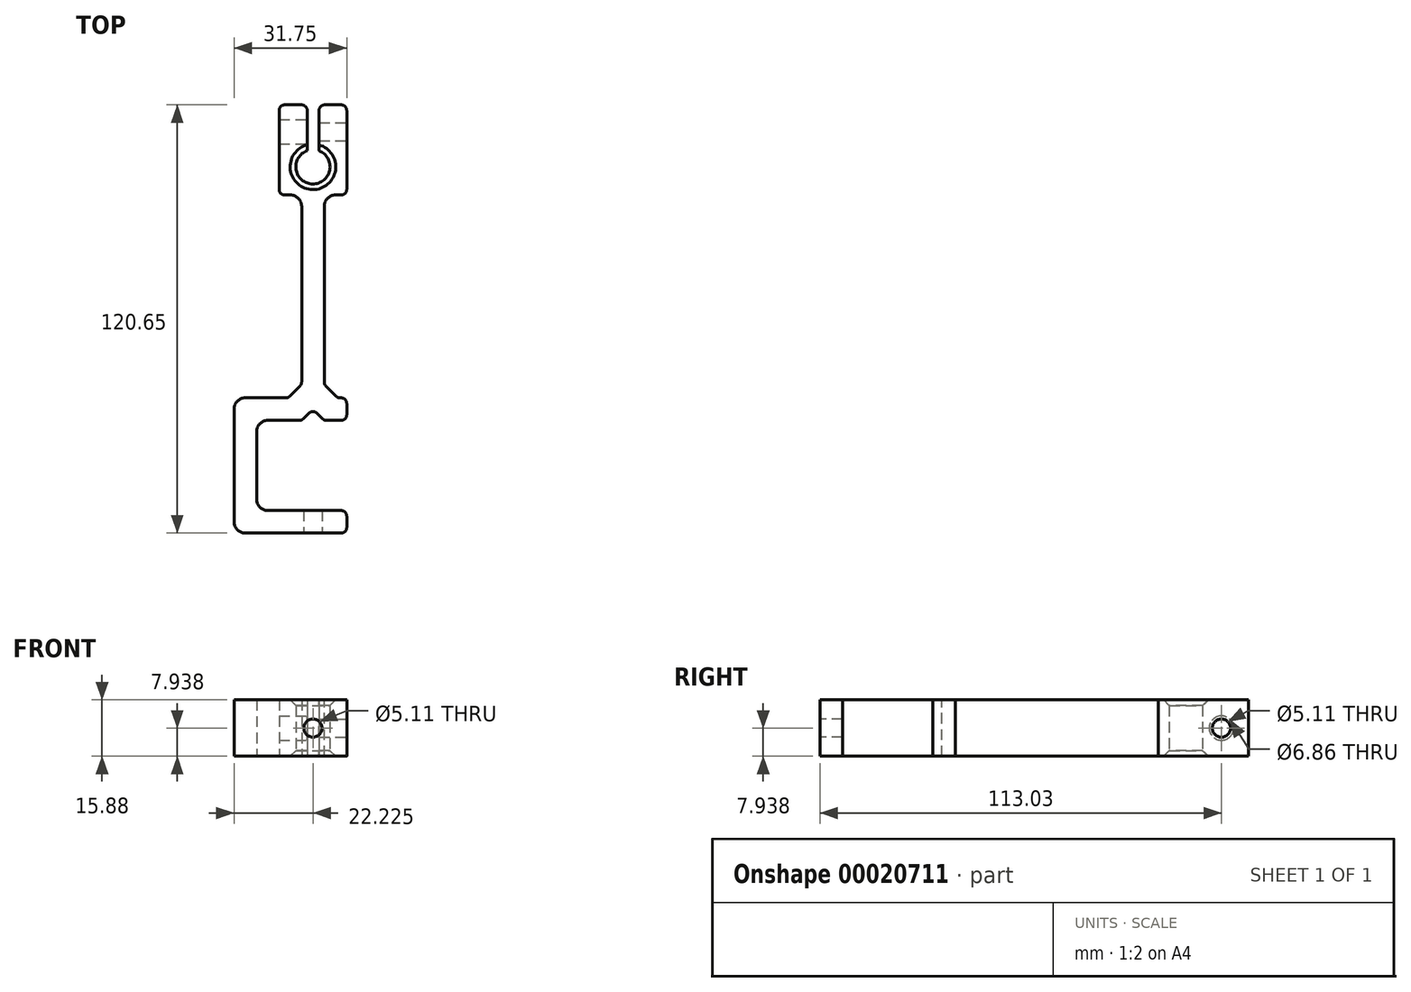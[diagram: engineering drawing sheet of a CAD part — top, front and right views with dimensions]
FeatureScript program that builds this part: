
annotation { "Feature Type Name" : "Feature", "Feature Type Description" : "" }
export const myFeature = defineFeature(function(context is Context, id is Id, definition is map)
    precondition{}
    {
        {
            var Q0;
            Q0=qCreatedBy(makeId("Top.planeOp"),FACE);
            var sketch = newSketch(context, id + "F0", { "sketchPlane" : qUnion([Q0])});
            skLineSegment(sketch, "E0", {"start": v(0, 0) * mm, "end": v(0, 31.75) * mm});
            skLineSegment(sketch, "E1", {"start": v(6.35, 111.12) * mm, "end": v(6.35, 95.25) * mm});
            skLineSegment(sketch, "E2", {"start": v(-6.35, 38.1) * mm, "end": v(-6.35, 0) * mm});
            skLineSegment(sketch, "E3", {"start": v(-6.35, 0) * mm, "end": v(0, 0) * mm});
            skArc(sketch, "E4", {"start": v(14.29, 107.74) * mm, "mid": v(15.8, 98.36) * mm, "end": v(17.59, 107.7) * mm});
            skLineSegment(sketch, "E5", {"start": v(6.35, 95.25) * mm, "end": v(12.7, 95.25) * mm});
            skLineSegment(sketch, "E6", {"start": v(12.7, 95.25) * mm, "end": v(12.7, 38.1) * mm});
            skLineSegment(sketch, "E7", {"start": v(25.4, 95.25) * mm, "end": v(19.05, 95.25) * mm});
            skLineSegment(sketch, "E8.trimOffspring", {"start": v(25.4, 95.25) * mm, "end": v(25.4, 111.12) * mm});
            skLineSegment(sketch, "E9", {"start": v(12.7, 38.1) * mm, "end": v(-6.35, 38.1) * mm});
            skLineSegment(sketch, "E10", {"start": v(19.05, 95.25) * mm, "end": v(19.05, 38.1) * mm});
            skLineSegment(sketch, "E11", {"start": v(6.35, 111.12) * mm, "end": v(6.35, 120.65) * mm});
            skLineSegment(sketch, "E12", {"start": v(6.35, 120.65) * mm, "end": v(14.29, 120.65) * mm});
            skLineSegment(sketch, "E13", {"start": v(25.4, 120.65) * mm, "end": v(25.4, 111.12) * mm});
            skLineSegment(sketch, "E14", {"start": v(14.29, 120.65) * mm, "end": v(14.29, 107.74) * mm});
            skLineSegment(sketch, "E15", {"start": v(17.59, 120.65) * mm, "end": v(17.59, 107.7) * mm});
            skLineSegment(sketch, "E16.trimOffspring", {"start": v(17.59, 120.65) * mm, "end": v(25.4, 120.65) * mm});
            skLineSegment(sketch, "E17", {"start": v(19.05, 38.1) * mm, "end": v(25.4, 38.1) * mm});
            skLineSegment(sketch, "E18", {"start": v(25.4, 38.1) * mm, "end": v(25.4, 31.75) * mm});
            skLineSegment(sketch, "E19", {"start": v(0, 0) * mm, "end": v(25.4, 0) * mm});
            skLineSegment(sketch, "E20", {"start": v(25.4, 0) * mm, "end": v(25.4, 6.35) * mm});
            skLineSegment(sketch, "E21", {"start": v(25.4, 6.35) * mm, "end": v(0, 6.35) * mm});
            skLineSegment(sketch, "E22", {"start": v(0, 31.75) * mm, "end": v(12.7, 31.75) * mm});
            skLineSegment(sketch, "E23", {"start": v(12.7, 31.75) * mm, "end": v(15.88, 34.92) * mm});
            skLineSegment(sketch, "E24", {"start": v(15.88, 34.92) * mm, "end": v(19.05, 31.75) * mm});
            skLineSegment(sketch, "E25", {"start": v(19.05, 31.75) * mm, "end": v(25.4, 31.75) * mm});
            skSolve(sketch);
        }
        {
            var Q0;
            Q0=qSketchRegion(id+"F0",true);
            extrude(context, id + "F1", {"entities" : qUnion([Q0]), "depth" : 15.88 * mm});
        }
        {
            var Q0;
            Q0=makeQuery(id+"F1.opExtrude","SWEPT_EDGE",EDGE,{"disambiguationData":[OSD([sQuery(id+"F0.wireOp",EDGE,"E0"),sQuery(id+"F0.wireOp",EDGE,"cbf15064-4b03-4c0a-8a49-597fd69c5e20.trimOffspring")])]});
            var Q1;
            Q1=makeQuery(id+"F1.opExtrude","SWEPT_EDGE",EDGE,{"disambiguationData":[OSD([sQuery(id+"F0.wireOp",EDGE,"E0"),sQuery(id+"F0.wireOp",EDGE,"E21")])]});
            var Q2;
            Q2=makeQuery(id+"F1.opExtrude","SWEPT_EDGE",EDGE,{"disambiguationData":[OSD([sQuery(id+"F0.wireOp",EDGE,"E5"),sQuery(id+"F0.wireOp",EDGE,"E6")])]});
            var Q3;
            Q3=makeQuery(id+"F1.opExtrude","SWEPT_EDGE",EDGE,{"disambiguationData":[OSD([sQuery(id+"F0.wireOp",EDGE,"E7"),sQuery(id+"F0.wireOp",EDGE,"E10")])]});
            var Q4;
            Q4=makeQuery(id+"F1.opExtrude","SWEPT_EDGE",EDGE,{"disambiguationData":[OSD([sQuery(id+"F0.wireOp",EDGE,"E2"),sQuery(id+"F0.wireOp",EDGE,"E9")])]});
            var Q5;
            Q5=makeQuery(id+"F1.opExtrude","SWEPT_EDGE",EDGE,{"disambiguationData":[OSD([sQuery(id+"F0.wireOp",EDGE,"E2"),sQuery(id+"F0.wireOp",EDGE,"E3")])]});
            fillet(context, id + "F2", {"entities" : qUnion([Q0, Q1, Q2, Q3, Q4, Q5]), "radius" : 3.17 * mm, "tangentPropagation" : true, "allowEdgeOverflow" : false});
        }
        {
            var Q0;
            Q0=makeQuery(id+"F1.opExtrude","SWEPT_FACE",FACE,{"disambiguationData":[OSD([sQuery(id+"F0.wireOp",EDGE,"E8.trimOffspring")])]});
            var sketch = newSketch(context, id + "F3", { "sketchPlane" : qUnion([Q0])});
            skCircle(sketch, "E26", {"center": v(113.03, 7.94) * mm, "radius": 2.55 * mm});
            skSolve(sketch);
        }
        {
            var Q0;
            Q0=qSketchRegion(id+"F3",true);
            extrude(context, id + "F4", {"entities" : qUnion([Q0]), "operationType" : NewBodyOperationType.REMOVE, "endBound" : BoundingType.UP_TO_NEXT, "oppositeDirection" : true, "depth" : 6.35 * mm});
        }
        {
            var Q0;
            Q0=makeQuery(id+"F1.opExtrude","CAP_EDGE",EDGE,{"disambiguationData":[OSD([sQuery(id+"F0.wireOp",EDGE,"E4")])],"isStart":false});
            var Q1;
            Q1=makeQuery(id+"F1.opExtrude","CAP_EDGE",EDGE,{"disambiguationData":[OSD([sQuery(id+"F0.wireOp",EDGE,"E4")])],"isStart":true});
            chamfer(context, id + "F5", {"entities" : qUnion([Q0, Q1]), "width" : 1.59 * mm, "tangentPropagation" : true});
        }
        {
            var Q0;
            Q0=makeQuery(id+"F1.opExtrude","SWEPT_FACE",FACE,{"disambiguationData":[OSD([sQuery(id+"F0.wireOp",EDGE,"E14")])]});
            var sketch = newSketch(context, id + "F6", { "sketchPlane" : qUnion([Q0])});
            skCircle(sketch, "E27", {"center": v(113.03, 7.94) * mm, "radius": 3.43 * mm});
            skSolve(sketch);
        }
        {
            var Q0;
            Q0=makeQuery(id+"F6.imprint","IMPRINT",FACE,{"disambiguationData":[TD([[makeQuery(id+"F6.imprint","IMPRINT",EDGE,{"derivedFrom":sQuery(id+"F6.wireOp",EDGE,"E27")}),1.0]])]});
            extrude(context, id + "F7", {"entities" : qUnion([Q0]), "operationType" : NewBodyOperationType.REMOVE, "oppositeDirection" : true, "depth" : 25.4 * mm});
        }
        {
            var Q0;
            Q0=makeQuery(id+"F1.opExtrude","SWEPT_FACE",FACE,{"disambiguationData":[OSD([sQuery(id+"F0.wireOp",EDGE,"E3"),sQuery(id+"F0.wireOp",EDGE,"E19")])]});
            var sketch = newSketch(context, id + "F8", { "sketchPlane" : qUnion([Q0])});
            skCircle(sketch, "E28", {"center": v(15.88, 7.94) * mm, "radius": 2.55 * mm});
            skSolve(sketch);
        }
        {
            var Q0;
            Q0 = qSketchRegion(id + "F8", true);
            extrude(context, id + "F9", {"entities" : qUnion([Q0]), "operationType" : NewBodyOperationType.REMOVE, "oppositeDirection" : true, "depth" : 12.7 * mm});
        }
        {
            var Q0;
            Q0=makeQuery(id+"F1.opExtrude","SWEPT_EDGE",EDGE,{"disambiguationData":[OSD([sQuery(id+"F0.wireOp",EDGE,"50a2365a-619f-4fc1-918a-f18a69e42369"),sQuery(id+"F0.wireOp",EDGE,"369a431b-04ca-40ed-8f71-0de861f8cea2")])]});
            var Q1;
            Q1=makeQuery(id+"F1.opExtrude","SWEPT_EDGE",EDGE,{"disambiguationData":[OSD([sQuery(id+"F0.wireOp",EDGE,"E23"),sQuery(id+"F0.wireOp",EDGE,"E24")])]});
            var Q2;
            Q2=makeQuery(id+"F1.opExtrude","SWEPT_EDGE",EDGE,{"disambiguationData":[OSD([sQuery(id+"F0.wireOp",EDGE,"E22"),sQuery(id+"F0.wireOp",EDGE,"E23")])]});
            var Q3;
            Q3=makeQuery(id+"F1.opExtrude","SWEPT_EDGE",EDGE,{"disambiguationData":[OSD([sQuery(id+"F0.wireOp",EDGE,"E24"),sQuery(id+"F0.wireOp",EDGE,"E25")])]});
            fillet(context, id + "F10", {"entities" : qUnion([Q0, Q1, Q2, Q3]), "radius" : 1.59 * mm, "tangentPropagation" : true, "allowEdgeOverflow" : false});
        }
        {
            var Q0;
            Q0=makeQuery(id+"F1.opExtrude","SWEPT_EDGE",EDGE,{"disambiguationData":[OSD([sQuery(id+"F0.wireOp",EDGE,"E10"),sQuery(id+"F0.wireOp",EDGE,"E17")])]});
            var Q1;
            Q1=makeQuery(id+"F1.opExtrude","SWEPT_EDGE",EDGE,{"disambiguationData":[OSD([sQuery(id+"F0.wireOp",EDGE,"E6"),sQuery(id+"F0.wireOp",EDGE,"E9")])]});
            chamfer(context, id + "F11", {"entities" : qUnion([Q0, Q1]), "width" : 3.8 * mm, "tangentPropagation" : true});
        }
        {
            var Q0;
            Q0=makeQuery(id+"F1.opExtrude","SWEPT_EDGE",EDGE,{"disambiguationData":[OSD([sQuery(id+"F0.wireOp",EDGE,"E7"),sQuery(id+"F0.wireOp",EDGE,"E8.trimOffspring")])]});
            var Q1;
            Q1=makeQuery(id+"F1.opExtrude","SWEPT_EDGE",EDGE,{"disambiguationData":[OSD([sQuery(id+"F0.wireOp",EDGE,"E1"),sQuery(id+"F0.wireOp",EDGE,"E5")])]});
            var Q2;
            Q2=makeQuery(id+"F1.opExtrude","SWEPT_EDGE",EDGE,{"disambiguationData":[OSD([sQuery(id+"F0.wireOp",EDGE,"E13"),sQuery(id+"F0.wireOp",EDGE,"E16.trimOffspring")])]});
            var Q3;
            Q3=makeQuery(id+"F1.opExtrude","SWEPT_EDGE",EDGE,{"disambiguationData":[OSD([sQuery(id+"F0.wireOp",EDGE,"E11"),sQuery(id+"F0.wireOp",EDGE,"E12")])]});
            var Q4;
            Q4=makeQuery(id+"F1.opExtrude","SWEPT_EDGE",EDGE,{"disambiguationData":[OSD([sQuery(id+"F0.wireOp",EDGE,"E15"),sQuery(id+"F0.wireOp",EDGE,"E16.trimOffspring")])]});
            var Q5;
            Q5=makeQuery(id+"F1.opExtrude","SWEPT_EDGE",EDGE,{"disambiguationData":[OSD([sQuery(id+"F0.wireOp",EDGE,"E12"),sQuery(id+"F0.wireOp",EDGE,"E14")])]});
            var Q6;
            Q6=makeQuery(id+"F1.opExtrude","SWEPT_EDGE",EDGE,{"disambiguationData":[OSD([sQuery(id+"F0.wireOp",EDGE,"E18"),sQuery(id+"F0.wireOp",EDGE,"791b4465-8142-4bf7-92e1-a9d28a65c818")])]});
            var Q7;
            Q7=makeQuery(id+"F1.opExtrude","SWEPT_EDGE",EDGE,{"disambiguationData":[OSD([sQuery(id+"F0.wireOp",EDGE,"E20"),sQuery(id+"F0.wireOp",EDGE,"E21")])]});
            var Q8;
            Q8=makeQuery(id+"F1.opExtrude","SWEPT_EDGE",EDGE,{"disambiguationData":[OSD([sQuery(id+"F0.wireOp",EDGE,"E17"),sQuery(id+"F0.wireOp",EDGE,"E18")])]});
            var Q9;
            Q9=makeQuery(id+"F1.opExtrude","SWEPT_EDGE",EDGE,{"disambiguationData":[OSD([sQuery(id+"F0.wireOp",EDGE,"E19"),sQuery(id+"F0.wireOp",EDGE,"E20")])]});
            var Q10;
            Q10=makeQuery(id+"F1.opExtrude","SWEPT_EDGE",EDGE,{"disambiguationData":[OSD([sQuery(id+"F0.wireOp",EDGE,"50a2365a-619f-4fc1-918a-f18a69e42369"),sQuery(id+"F0.wireOp",EDGE,"cbf15064-4b03-4c0a-8a49-597fd69c5e20.trimOffspring")])]});
            var Q11;
            Q11=makeQuery(id+"F1.opExtrude","SWEPT_EDGE",EDGE,{"disambiguationData":[OSD([sQuery(id+"F0.wireOp",EDGE,"791b4465-8142-4bf7-92e1-a9d28a65c818"),sQuery(id+"F0.wireOp",EDGE,"369a431b-04ca-40ed-8f71-0de861f8cea2")])]});
            var Q12;
            {var subQ0=sQuery(id+"F0.wireOp",EDGE,"E9");Q12=makeQuery(id+"F11.opChamfer","BLEND_EDGE",EDGE,{"blendedFrom":[makeQuery(id+"F1.opExtrude","SWEPT_EDGE",EDGE,{"disambiguationData":[OSD([sQuery(id+"F0.wireOp",EDGE,"E6"),subQ0])]}),makeQuery(id+"F1.opExtrude","SWEPT_FACE",FACE,{"disambiguationData":[OSD([subQ0])]})],"blendedInto":[makeQuery(id+"F1.opExtrude","SWEPT_FACE",FACE,{"disambiguationData":[OSD([subQ0])]})]});}
            var Q13;
            {var subQ0=sQuery(id+"F0.wireOp",EDGE,"E6");Q13=makeQuery(id+"F11.opChamfer","BLEND_EDGE",EDGE,{"blendedFrom":[makeQuery(id+"F1.opExtrude","SWEPT_EDGE",EDGE,{"disambiguationData":[OSD([subQ0,sQuery(id+"F0.wireOp",EDGE,"E9")])]}),makeQuery(id+"F1.opExtrude","SWEPT_FACE",FACE,{"disambiguationData":[OSD([subQ0])]})],"blendedInto":[makeQuery(id+"F1.opExtrude","SWEPT_FACE",FACE,{"disambiguationData":[OSD([subQ0])]})]});}
            var Q14;
            {var subQ0=sQuery(id+"F0.wireOp",EDGE,"E10");Q14=makeQuery(id+"F11.opChamfer","BLEND_EDGE",EDGE,{"blendedFrom":[makeQuery(id+"F1.opExtrude","SWEPT_EDGE",EDGE,{"disambiguationData":[OSD([subQ0,sQuery(id+"F0.wireOp",EDGE,"E17")])]}),makeQuery(id+"F1.opExtrude","SWEPT_FACE",FACE,{"disambiguationData":[OSD([subQ0])]})],"blendedInto":[makeQuery(id+"F1.opExtrude","SWEPT_FACE",FACE,{"disambiguationData":[OSD([subQ0])]})]});}
            var Q15;
            {var subQ0=sQuery(id+"F0.wireOp",EDGE,"E17");Q15=makeQuery(id+"F11.opChamfer","BLEND_EDGE",EDGE,{"blendedFrom":[makeQuery(id+"F1.opExtrude","SWEPT_EDGE",EDGE,{"disambiguationData":[OSD([sQuery(id+"F0.wireOp",EDGE,"E10"),subQ0])]}),makeQuery(id+"F1.opExtrude","SWEPT_FACE",FACE,{"disambiguationData":[OSD([subQ0])]})],"blendedInto":[makeQuery(id+"F1.opExtrude","SWEPT_FACE",FACE,{"disambiguationData":[OSD([subQ0])]})]});}
            fillet(context, id + "F12", {"entities" : qUnion([Q0, Q1, Q2, Q3, Q4, Q5, Q6, Q7, Q8, Q9, Q10, Q11, Q12, Q13, Q14, Q15]), "radius" : 1.59 * mm, "tangentPropagation" : true, "allowEdgeOverflow" : false});
        }
    });
